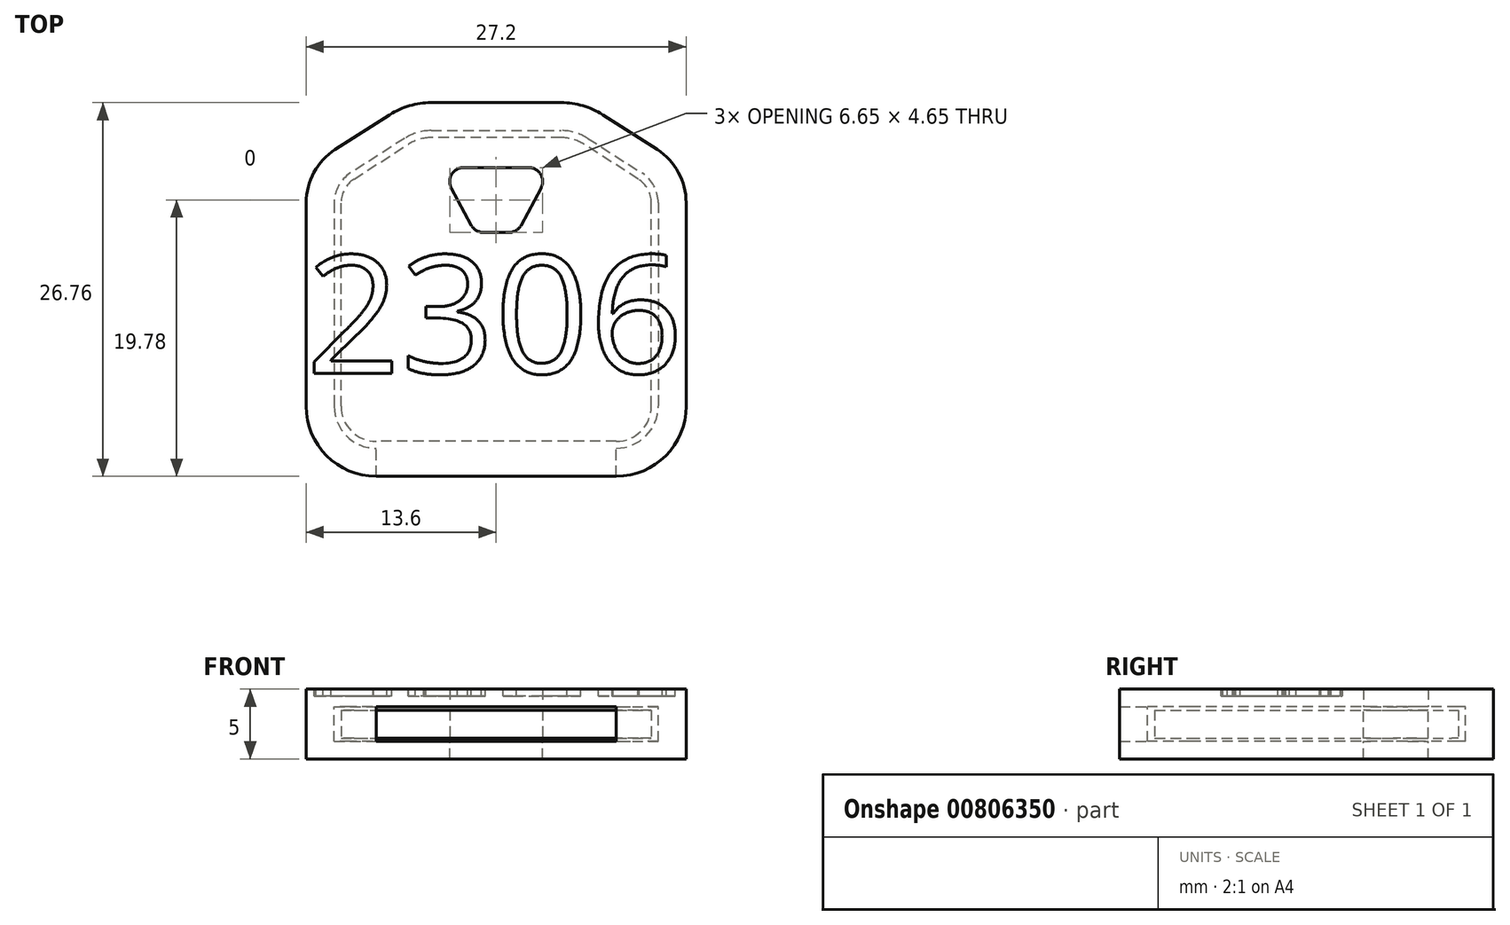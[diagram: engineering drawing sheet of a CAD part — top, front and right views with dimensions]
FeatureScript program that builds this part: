
annotation { "Feature Type Name" : "Feature", "Feature Type Description" : "" }
export const myFeature = defineFeature(function(context is Context, id is Id, definition is map)
    precondition{}
    {
        {
            var Q0;
            Q0=qCreatedBy(makeId("Top.planeOp"),FACE);
            var sketch = newSketch(context, id + "F0", { "sketchPlane" : qUnion([Q0])});
            skLineSegment(sketch, "E0.bottom", {"start": v(11.1, -10.88) * mm, "end": v(-11.1, -10.88) * mm});
            skLineSegment(sketch, "E0.top", {"start": v(11.1, 10.88) * mm, "end": v(-11.1, 10.87) * mm});
            skLineSegment(sketch, "E0.left", {"start": v(11.1, -10.88) * mm, "end": v(11.1, 10.88) * mm});
            skLineSegment(sketch, "E0.right", {"start": v(-11.1, -10.88) * mm, "end": v(-11.1, 10.88) * mm});
            skPoint(sketch, "E0.middle", {"position": v(0, 0) * mm});
            skLineSegment(sketch, "E1", {"start": v(-11.1, 7.31) * mm, "end": v(-5.54, 10.87) * mm});
            skLineSegment(sketch, "E2.MirrorCS", {"start": v(11.1, 7.31) * mm, "end": v(5.54, 10.87) * mm});
            skSolve(sketch);
        }
        {
            var Q0;
            {var subQ1=sQuery(id+"F0.wireOp",EDGE,"E0.bottom");Q0=makeQuery(id+"F0.imprint","IMPRINT",FACE,{"disambiguationData":[TD([[makeQuery(id+"F0.imprint","IMPRINT",EDGE,{"derivedFrom":subQ1}),-1.0]])]});}
            extrude(context, id + "F1", {"entities" : qUnion([Q0]), "endBound" : BoundingType.SYMMETRIC, "depth" : 2 * mm, "offsetDistance" : 25 * mm});
        }
        {
            var Q0;
            Q0=makeQuery(id+"F1.opExtrude","SWEPT_EDGE",EDGE,{"disambiguationData":[OSD([sQuery(id+"F0.wireOp",EDGE,"E0.top"),sQuery(id+"F0.wireOp",EDGE,"E1")])]});
            var Q1;
            Q1=makeQuery(id+"F1.opExtrude","SWEPT_EDGE",EDGE,{"disambiguationData":[OSD([sQuery(id+"F0.wireOp",EDGE,"E0.top"),sQuery(id+"F0.wireOp",EDGE,"E2.MirrorCS")])]});
            fillet(context, id + "F2", {"entities" : qUnion([Q0, Q1]), "radius" : 3 * mm, "tangentPropagation" : true, "allowEdgeOverflow" : false});
        }
        {
            var Q0;
            Q0=makeQuery(id+"F1.opExtrude","SWEPT_EDGE",EDGE,{"disambiguationData":[OSD([sQuery(id+"F0.wireOp",EDGE,"E0.right"),sQuery(id+"F0.wireOp",EDGE,"E1")])]});
            var Q1;
            Q1=makeQuery(id+"F1.opExtrude","SWEPT_EDGE",EDGE,{"disambiguationData":[OSD([sQuery(id+"F0.wireOp",EDGE,"E0.left"),sQuery(id+"F0.wireOp",EDGE,"E2.MirrorCS")])]});
            fillet(context, id + "F3", {"entities" : qUnion([Q0, Q1]), "radius" : 2 * mm, "tangentPropagation" : true, "allowEdgeOverflow" : false});
        }
        {
            var Q0;
            Q0=makeQuery(id+"F1.opExtrude","SWEPT_EDGE",EDGE,{"disambiguationData":[OSD([sQuery(id+"F0.wireOp",EDGE,"E0.bottom"),sQuery(id+"F0.wireOp",EDGE,"E0.right")])]});
            var Q1;
            Q1=makeQuery(id+"F1.opExtrude","SWEPT_EDGE",EDGE,{"disambiguationData":[OSD([sQuery(id+"F0.wireOp",EDGE,"E0.bottom"),sQuery(id+"F0.wireOp",EDGE,"E0.left")])]});
            fillet(context, id + "F4", {"entities" : qUnion([Q0, Q1]), "radius" : 2.5 * mm, "tangentPropagation" : true, "allowEdgeOverflow" : false});
        }
        {
            var Q0;
            Q0=makeQuery(id+"F1.opExtrude","CAP_FACE",FACE,{"disambiguationData":[OSD([sQuery(id+"F0.wireOp",EDGE,"E0.bottom"),sQuery(id+"F0.wireOp",EDGE,"E0.top"),sQuery(id+"F0.wireOp",EDGE,"E0.left"),sQuery(id+"F0.wireOp",EDGE,"E0.right"),sQuery(id+"F0.wireOp",EDGE,"E1"),sQuery(id+"F0.wireOp",EDGE,"E2.MirrorCS")])],"isStart":false});
            var sketch = newSketch(context, id + "F5", { "sketchPlane" : qUnion([Q0])});
            skLineSegment(sketch, "E3", {"start": v(-4, 8.72) * mm, "end": v(4, 8.72) * mm});
            skLineSegment(sketch, "E4", {"start": v(-1.5, 4.07) * mm, "end": v(1.5, 4.07) * mm});
            skLineSegment(sketch, "E5", {"start": v(-1.5, 4.07) * mm, "end": v(-4, 8.72) * mm});
            skLineSegment(sketch, "E6", {"start": v(4, 8.72) * mm, "end": v(1.5, 4.08) * mm});
            skSolve(sketch);
        }
        {
            var Q0;
            Q0=makeQuery(id+"F5.imprint","IMPRINT",FACE,{"disambiguationData":[TD([[makeQuery(id+"F5.imprint","IMPRINT",EDGE,{"derivedFrom":sQuery(id+"F5.wireOp",EDGE,"E3")}),-1.0]])]});
            extrude(context, id + "F6", {"entities" : qUnion([Q0]), "operationType" : NewBodyOperationType.REMOVE, "oppositeDirection" : true, "depth" : 25 * mm, "offsetDistance" : 25 * mm});
        }
        {
            var Q0;
            Q0=makeQuery(id+"F6.boolean.opBoolean","COPY",EDGE,{"derivedFrom":makeQuery(id+"F6.opExtrude","SWEPT_EDGE",EDGE,{"disambiguationData":[OSD([sQuery(id+"F5.wireOp",EDGE,"E3"),sQuery(id+"F5.wireOp",EDGE,"E5")])]})});
            var Q1;
            Q1=makeQuery(id+"F6.boolean.opBoolean","COPY",EDGE,{"derivedFrom":makeQuery(id+"F6.opExtrude","SWEPT_EDGE",EDGE,{"disambiguationData":[OSD([sQuery(id+"F5.wireOp",EDGE,"E3"),sQuery(id+"F5.wireOp",EDGE,"E6")])]})});
            fillet(context, id + "F7", {"entities" : qUnion([Q0, Q1]), "radius" : 1 * mm, "tangentPropagation" : true, "allowEdgeOverflow" : false});
        }
        {
            var Q0;
            Q0=makeQuery(id+"F6.boolean.opBoolean","COPY",EDGE,{"derivedFrom":makeQuery(id+"F6.opExtrude","SWEPT_EDGE",EDGE,{"disambiguationData":[OSD([sQuery(id+"F5.wireOp",EDGE,"E4"),sQuery(id+"F5.wireOp",EDGE,"E5")])]})});
            var Q1;
            Q1=makeQuery(id+"F6.boolean.opBoolean","COPY",EDGE,{"derivedFrom":makeQuery(id+"F6.opExtrude","SWEPT_EDGE",EDGE,{"disambiguationData":[OSD([sQuery(id+"F5.wireOp",EDGE,"E4"),sQuery(id+"F5.wireOp",EDGE,"E6")])]})});
            fillet(context, id + "F8", {"entities" : qUnion([Q0, Q1]), "radius" : 1 * mm, "tangentPropagation" : true, "allowEdgeOverflow" : false});
        }
        {
            var Q0;
            Q0=makeQuery(id+"F1.opExtrude","CAP_FACE",FACE,{"disambiguationData":[OSD([sQuery(id+"F0.wireOp",EDGE,"E0.bottom"),sQuery(id+"F0.wireOp",EDGE,"E0.top"),sQuery(id+"F0.wireOp",EDGE,"E0.left"),sQuery(id+"F0.wireOp",EDGE,"E0.right"),sQuery(id+"F0.wireOp",EDGE,"E1"),sQuery(id+"F0.wireOp",EDGE,"E2.MirrorCS")])],"isStart":false});
            var sketch = newSketch(context, id + "F9", { "sketchPlane" : qUnion([Q0])});
            skArc(sketch, "E7.0", {"start": v(-11.53, 10.01) * mm, "mid": v(-13.05, 8.38) * mm, "end": v(-13.6, 6.22) * mm});
            skLineSegment(sketch, "E7.1", {"start": v(11.53, 10.01) * mm, "end": v(7.63, 12.5) * mm});
            skArc(sketch, "E7.2", {"start": v(7.63, 12.5) * mm, "mid": v(6.2, 13.15) * mm, "end": v(4.66, 13.37) * mm});
            skLineSegment(sketch, "E7.3", {"start": v(4.66, 13.37) * mm, "end": v(-4.66, 13.37) * mm});
            skArc(sketch, "E7.4", {"start": v(-4.66, 13.37) * mm, "mid": v(-6.2, 13.15) * mm, "end": v(-7.63, 12.5) * mm});
            skArc(sketch, "E7.5", {"start": v(13.6, 6.22) * mm, "mid": v(13.05, 8.38) * mm, "end": v(11.53, 10.01) * mm});
            skLineSegment(sketch, "E7.6", {"start": v(-11.53, 10.01) * mm, "end": v(-7.63, 12.5) * mm});
            skLineSegment(sketch, "E7.7", {"start": v(13.6, -8.37) * mm, "end": v(13.6, 6.22) * mm});
            skArc(sketch, "E7.8", {"start": v(8.6, -13.37) * mm, "mid": v(12.14, -11.91) * mm, "end": v(13.6, -8.37) * mm});
            skLineSegment(sketch, "E7.9", {"start": v(8.6, -13.37) * mm, "end": v(-8.6, -13.38) * mm});
            skArc(sketch, "E7.10", {"start": v(-13.6, -8.38) * mm, "mid": v(-12.14, -11.91) * mm, "end": v(-8.6, -13.38) * mm});
            skLineSegment(sketch, "E7.11", {"start": v(-13.6, -8.38) * mm, "end": v(-13.6, 6.22) * mm});
            skArc(sketch, "E8.0", {"start": v(-10.45, 8.33) * mm, "mid": v(-11.3, 7.42) * mm, "end": v(-11.6, 6.22) * mm});
            skLineSegment(sketch, "E8.1", {"start": v(10.45, 8.33) * mm, "end": v(6.55, 10.82) * mm});
            skArc(sketch, "E8.2", {"start": v(6.55, 10.82) * mm, "mid": v(5.65, 11.23) * mm, "end": v(4.66, 11.38) * mm});
            skLineSegment(sketch, "E8.3", {"start": v(4.66, 11.38) * mm, "end": v(-4.66, 11.38) * mm});
            skArc(sketch, "E8.4", {"start": v(-4.66, 11.38) * mm, "mid": v(-5.65, 11.23) * mm, "end": v(-6.55, 10.82) * mm});
            skArc(sketch, "E8.5", {"start": v(11.6, 6.22) * mm, "mid": v(11.3, 7.42) * mm, "end": v(10.45, 8.33) * mm});
            skLineSegment(sketch, "E8.6", {"start": v(-10.45, 8.33) * mm, "end": v(-6.55, 10.82) * mm});
            skLineSegment(sketch, "E8.7", {"start": v(11.6, -8.37) * mm, "end": v(11.6, 6.22) * mm});
            skArc(sketch, "E8.8", {"start": v(8.6, -11.38) * mm, "mid": v(10.72, -10.5) * mm, "end": v(11.6, -8.37) * mm});
            skLineSegment(sketch, "E8.9", {"start": v(8.6, -11.38) * mm, "end": v(-8.6, -11.38) * mm});
            skArc(sketch, "E8.10", {"start": v(-11.6, -8.38) * mm, "mid": v(-10.72, -10.5) * mm, "end": v(-8.6, -11.38) * mm});
            skLineSegment(sketch, "E8.11", {"start": v(-11.6, -8.38) * mm, "end": v(-11.6, 6.22) * mm});
            skLineSegment(sketch, "E9.bottom", {"start": v(-8.6, -11.38) * mm, "end": v(8.6, -11.38) * mm});
            skLineSegment(sketch, "E9.top", {"start": v(-8.6, -13.37) * mm, "end": v(8.6, -13.37) * mm});
            skLineSegment(sketch, "E9.left", {"start": v(-8.6, -11.38) * mm, "end": v(-8.6, -13.37) * mm});
            skLineSegment(sketch, "E9.right", {"start": v(8.6, -11.38) * mm, "end": v(8.6, -13.37) * mm});
            skSolve(sketch);
        }
        {
            var Q0;
            Q0=makeQuery(id+"F9.imprint","IMPRINT",FACE,{"disambiguationData":[TD([[makeQuery(id+"F9.imprint","IMPRINT",EDGE,{"derivedFrom":sQuery(id+"F9.wireOp",EDGE,"E7.0")}),1.0]])]});
            extrude(context, id + "F10", {"entities" : qUnion([Q0]), "oppositeDirection" : true, "depth" : 3.5 * mm, "offsetDistance" : 25 * mm, "hasSecondDirection" : true, "secondDirectionOppositeDirection" : false, "secondDirectionDepth" : 1.5 * mm});
        }
        {
            var Q0;
            Q0=makeQuery(id+"F1.opExtrude","CAP_FACE",FACE,{"disambiguationData":[OSD([sQuery(id+"F0.wireOp",EDGE,"E0.bottom"),sQuery(id+"F0.wireOp",EDGE,"E0.top"),sQuery(id+"F0.wireOp",EDGE,"E0.left"),sQuery(id+"F0.wireOp",EDGE,"E0.right"),sQuery(id+"F0.wireOp",EDGE,"E1"),sQuery(id+"F0.wireOp",EDGE,"E2.MirrorCS")])],"isStart":false});
            var sketch = newSketch(context, id + "F11", { "sketchPlane" : qUnion([Q0])});
            skLineSegment(sketch, "E10.0", {"start": v(-13.6, -8.38) * mm, "end": v(-13.6, 6.22) * mm});
            skArc(sketch, "E10.1", {"start": v(13.6, 6.22) * mm, "mid": v(13.05, 8.38) * mm, "end": v(11.53, 10.01) * mm});
            skLineSegment(sketch, "E10.2", {"start": v(13.6, -8.37) * mm, "end": v(13.6, 6.22) * mm});
            skArc(sketch, "E10.3", {"start": v(8.6, -13.37) * mm, "mid": v(12.14, -11.91) * mm, "end": v(13.6, -8.37) * mm});
            skLineSegment(sketch, "E10.4", {"start": v(8.6, -13.37) * mm, "end": v(-8.6, -13.38) * mm});
            skLineSegment(sketch, "E10.5", {"start": v(11.53, 10.01) * mm, "end": v(7.63, 12.5) * mm});
            skArc(sketch, "E10.6", {"start": v(-13.6, -8.38) * mm, "mid": v(-12.14, -11.91) * mm, "end": v(-8.6, -13.38) * mm});
            skArc(sketch, "E10.7", {"start": v(7.63, 12.5) * mm, "mid": v(6.2, 13.15) * mm, "end": v(4.66, 13.38) * mm});
            skLineSegment(sketch, "E10.8", {"start": v(4.66, 13.37) * mm, "end": v(-4.66, 13.37) * mm});
            skArc(sketch, "E10.9", {"start": v(-4.66, 13.38) * mm, "mid": v(-6.2, 13.15) * mm, "end": v(-7.63, 12.5) * mm});
            skLineSegment(sketch, "E10.10", {"start": v(-11.53, 10.01) * mm, "end": v(-7.63, 12.5) * mm});
            skArc(sketch, "E10.11", {"start": v(-11.53, 10.01) * mm, "mid": v(-13.05, 8.38) * mm, "end": v(-13.6, 6.22) * mm});
            skSolve(sketch);
        }
        {
            var Q0;
            Q0=makeQuery(id+"F11.imprint","IMPRINT",FACE,{"disambiguationData":[TD([[makeQuery(id+"F11.imprint","IMPRINT",EDGE,{"derivedFrom":sQuery(id+"F11.wireOp",EDGE,"E10.0")}),-1.0]])]});
            var Q1;
            {var subQ5=sQuery(id+"F0.wireOp",EDGE,"E0.top");Q1=makeQuery(id+"F11.imprint","IMPRINT",FACE,{"disambiguationData":[TD([[makeQuery(id+"F11.imprint","IMPRINT",EDGE,{"derivedFrom":makeQuery(id+"F1.opExtrude","CAP_EDGE",EDGE,{"disambiguationData":[OSD([subQ5])],"isStart":false})}),1.0]])]});}
            extrude(context, id + "F12", {"entities" : qUnion([Q0, Q1]), "operationType" : NewBodyOperationType.ADD, "depth" : 1.5 * mm, "offsetDistance" : 25 * mm, "hasSecondDirection" : true, "secondDirectionOppositeDirection" : false, "secondDirectionDepth" : .25 * mm});
        }
        {
            var Q0;
            Q0=makeQuery(id+"F12.opExtrude","CAP_FACE",FACE,{"disambiguationData":[OSD([sQuery(id+"F0.wireOp",EDGE,"E0.bottom"),sQuery(id+"F0.wireOp",EDGE,"E0.top"),sQuery(id+"F0.wireOp",EDGE,"E0.left"),sQuery(id+"F0.wireOp",EDGE,"E0.right"),sQuery(id+"F0.wireOp",EDGE,"E1"),sQuery(id+"F0.wireOp",EDGE,"E2.MirrorCS"),sQuery(id+"F5.wireOp",EDGE,"E3"),sQuery(id+"F5.wireOp",EDGE,"E4"),sQuery(id+"F5.wireOp",EDGE,"E5"),sQuery(id+"F5.wireOp",EDGE,"E6"),sQuery(id+"F11.wireOp",EDGE,"E10.0"),sQuery(id+"F11.wireOp",EDGE,"E10.1"),sQuery(id+"F11.wireOp",EDGE,"E10.2"),sQuery(id+"F11.wireOp",EDGE,"E10.3"),sQuery(id+"F11.wireOp",EDGE,"E10.4"),sQuery(id+"F11.wireOp",EDGE,"E10.5"),sQuery(id+"F11.wireOp",EDGE,"E10.6"),sQuery(id+"F11.wireOp",EDGE,"E10.7"),sQuery(id+"F11.wireOp",EDGE,"E10.8"),sQuery(id+"F11.wireOp",EDGE,"E10.9"),sQuery(id+"F11.wireOp",EDGE,"E10.10"),sQuery(id+"F11.wireOp",EDGE,"E10.11")])],"isStart":true});
            extrude(context, id + "F13", {"entities" : qUnion([Q0]), "operationType" : NewBodyOperationType.ADD, "depth" : 3.75 * mm, "offsetDistance" : 25 * mm, "hasSecondDirection" : true, "secondDirectionOppositeDirection" : false, "secondDirectionDepth" : 2.5 * mm});
        }
        {
            var Q0;
            Q0=makeQuery(id+"F12.boolean.opBoolean","MERGE",FACE,{"derivedFrom":[makeQuery(id+"F10.opExtrude","CAP_FACE",FACE,{"disambiguationData":[OSD([sQuery(id+"F9.wireOp",EDGE,"E7.0"),sQuery(id+"F9.wireOp",EDGE,"E7.1"),sQuery(id+"F9.wireOp",EDGE,"E7.2"),sQuery(id+"F9.wireOp",EDGE,"E7.3"),sQuery(id+"F9.wireOp",EDGE,"E7.4"),sQuery(id+"F9.wireOp",EDGE,"E7.5"),sQuery(id+"F9.wireOp",EDGE,"E7.6"),sQuery(id+"F9.wireOp",EDGE,"E7.7"),sQuery(id+"F9.wireOp",EDGE,"E7.8"),sQuery(id+"F9.wireOp",EDGE,"E7.10"),sQuery(id+"F9.wireOp",EDGE,"E7.11"),sQuery(id+"F9.wireOp",EDGE,"E8.0"),sQuery(id+"F9.wireOp",EDGE,"E8.1"),sQuery(id+"F9.wireOp",EDGE,"E8.2"),sQuery(id+"F9.wireOp",EDGE,"E8.3"),sQuery(id+"F9.wireOp",EDGE,"E8.4"),sQuery(id+"F9.wireOp",EDGE,"E8.5"),sQuery(id+"F9.wireOp",EDGE,"E8.6"),sQuery(id+"F9.wireOp",EDGE,"E8.7"),sQuery(id+"F9.wireOp",EDGE,"E8.8"),sQuery(id+"F9.wireOp",EDGE,"E8.10"),sQuery(id+"F9.wireOp",EDGE,"E8.11"),sQuery(id+"F9.wireOp",EDGE,"E9.left"),sQuery(id+"F9.wireOp",EDGE,"E9.right")])],"isStart":true}),makeQuery(id+"F12.opExtrude","CAP_FACE",FACE,{"disambiguationData":[OSD([sQuery(id+"F0.wireOp",EDGE,"E0.bottom"),sQuery(id+"F0.wireOp",EDGE,"E0.top"),sQuery(id+"F0.wireOp",EDGE,"E0.left"),sQuery(id+"F0.wireOp",EDGE,"E0.right"),sQuery(id+"F0.wireOp",EDGE,"E1"),sQuery(id+"F0.wireOp",EDGE,"E2.MirrorCS"),sQuery(id+"F5.wireOp",EDGE,"E3"),sQuery(id+"F5.wireOp",EDGE,"E4"),sQuery(id+"F5.wireOp",EDGE,"E5"),sQuery(id+"F5.wireOp",EDGE,"E6"),sQuery(id+"F11.wireOp",EDGE,"E10.0"),sQuery(id+"F11.wireOp",EDGE,"E10.1"),sQuery(id+"F11.wireOp",EDGE,"E10.2"),sQuery(id+"F11.wireOp",EDGE,"E10.3"),sQuery(id+"F11.wireOp",EDGE,"E10.4"),sQuery(id+"F11.wireOp",EDGE,"E10.5"),sQuery(id+"F11.wireOp",EDGE,"E10.6"),sQuery(id+"F11.wireOp",EDGE,"E10.7"),sQuery(id+"F11.wireOp",EDGE,"E10.8"),sQuery(id+"F11.wireOp",EDGE,"E10.9"),sQuery(id+"F11.wireOp",EDGE,"E10.10"),sQuery(id+"F11.wireOp",EDGE,"E10.11")])],"isStart":false})]});
            var sketch = newSketch(context, id + "F14", { "sketchPlane" : qUnion([Q0])});
            skText(sketch, "E11", { "text": "2306\n", "fontName": "OpenSans-Regular.ttf"});
            const initialGuessF14  = {"E11": [-0.0136, -0.006, 1, 0, 0.0085]};
            skSetInitialGuess(sketch, initialGuessF14);
            skSolve(sketch);
        }
        {
            var Q0;
            Q0=makeQuery(id+"F14.imprint","IMPRINT",FACE,{"disambiguationData":[TD([[makeQuery(id+"F14.imprint","IMPRINT",EDGE,{"derivedFrom":sQuery(id+"F14.wireOp",EDGE,"E11.sketch_text.stroke-0")}),-1.0]])]});
            var Q1;
            Q1=makeQuery(id+"F14.imprint","IMPRINT",FACE,{"disambiguationData":[TD([[makeQuery(id+"F14.imprint","IMPRINT",EDGE,{"derivedFrom":sQuery(id+"F14.wireOp",EDGE,"E11.sketch_text.stroke-20")}),-1.0]])]});
            var Q2;
            Q2=makeQuery(id+"F14.imprint","IMPRINT",FACE,{"disambiguationData":[TD([[makeQuery(id+"F14.imprint","IMPRINT",EDGE,{"derivedFrom":sQuery(id+"F14.wireOp",EDGE,"E11.sketch_text.stroke-48")}),-1.0]])]});
            var Q3;
            Q3=makeQuery(id+"F14.imprint","IMPRINT",FACE,{"disambiguationData":[TD([[makeQuery(id+"F14.imprint","IMPRINT",EDGE,{"derivedFrom":sQuery(id+"F14.wireOp",EDGE,"E11.sketch_text.stroke-64")}),-1.0]])]});
            extrude(context, id + "F15", {"entities" : qUnion([Q0, Q1, Q2, Q3]), "operationType" : NewBodyOperationType.REMOVE, "oppositeDirection" : true, "depth" : .5 * mm, "offsetDistance" : 25 * mm});
        }
    });
